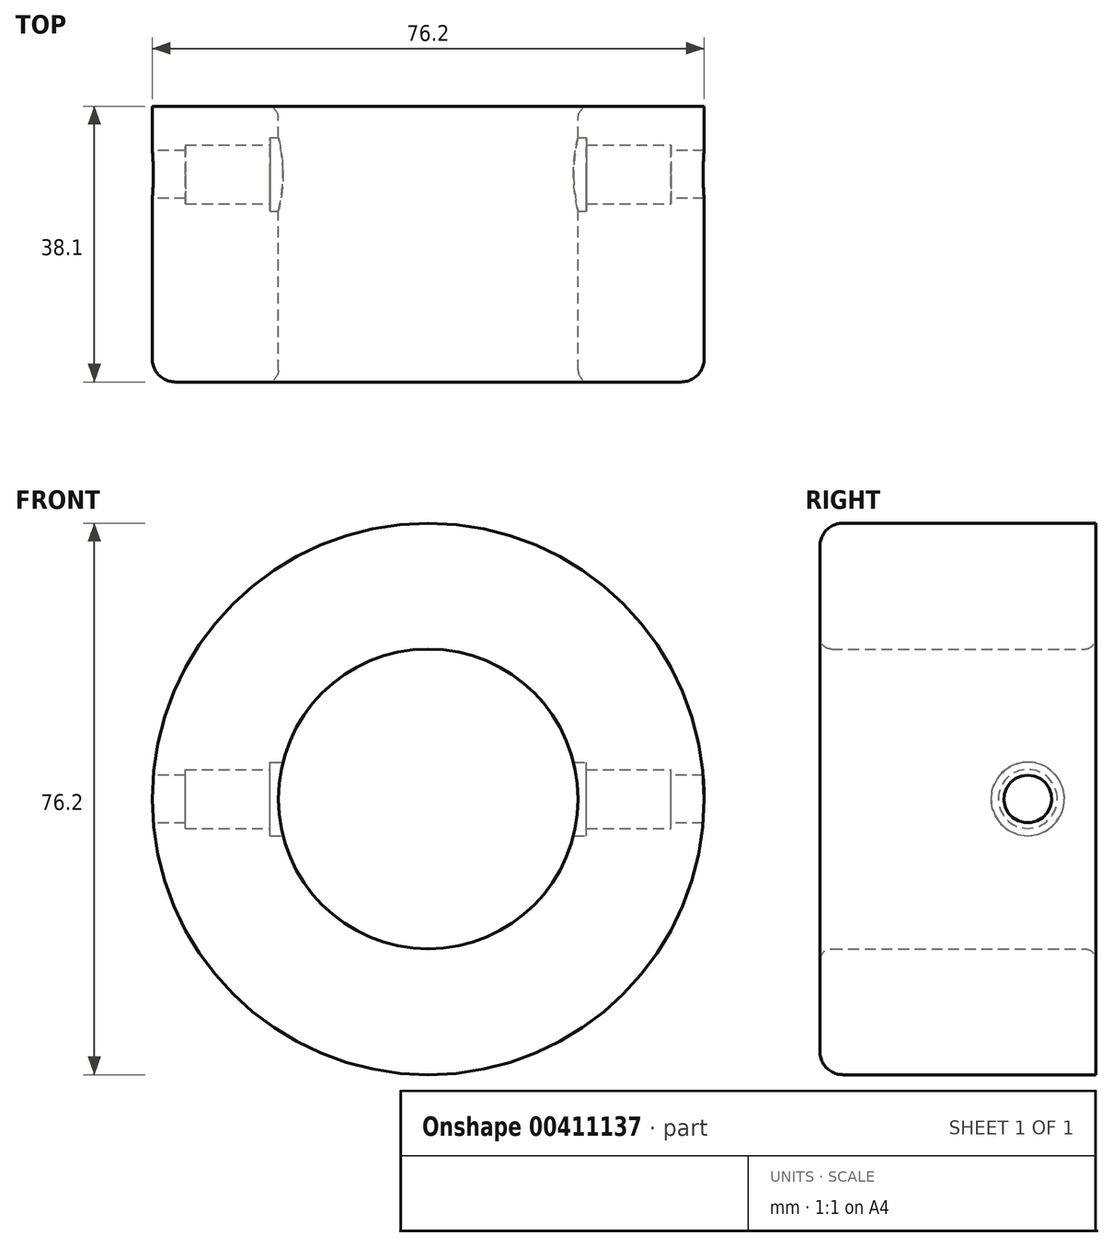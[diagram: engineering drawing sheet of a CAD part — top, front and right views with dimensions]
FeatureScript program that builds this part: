
annotation { "Feature Type Name" : "Feature", "Feature Type Description" : "" }
export const myFeature = defineFeature(function(context is Context, id is Id, definition is map)
    precondition{}
    {
        {
            var Q0;
            Q0=qCreatedBy(makeId("Front.planeOp"),FACE);
            var sketch = newSketch(context, id + "F0", { "sketchPlane" : qUnion([Q0])});
            skCircle(sketch, "E0", {"center": v(0, 0) * mm, "radius": 20.7 * mm});
            skCircle(sketch, "E1", {"center": v(0, 0) * mm, "radius": 38.1 * mm});
            skCircle(sketch, "E2", {"center": v(0, 0) * mm, "radius": 50.8 * mm});
            skSolve(sketch);
        }
        {
            var Q0;
            Q0=makeQuery(id+"F0.imprint","IMPRINT",FACE,{"disambiguationData":[TD([[makeQuery(id+"F0.imprint","IMPRINT",EDGE,{"derivedFrom":sQuery(id+"F0.wireOp",EDGE,"E0")}),-1.0]])]});
            extrude(context, id + "F1", {"entities" : qUnion([Q0]), "depth" : 38.1 * mm});
        }
        {
            var Q0;
            Q0=makeQuery(id+"F1.opExtrude","CAP_EDGE",EDGE,{"disambiguationData":[OSD([sQuery(id+"F0.wireOp",EDGE,"E1")])],"isStart":false});
            fillet(context, id + "F2", {"entities" : qUnion([Q0]), "radius" : 3.17 * mm, "tangentPropagation" : true, "allowEdgeOverflow" : false});
        }
        {
            var Q0;
            Q0=qCreatedBy(makeId("Right.planeOp"),FACE);
            var sketch = newSketch(context, id + "F3", { "sketchPlane" : qUnion([Q0])});
            skCircle(sketch, "E3", {"center": v(-9.4, 0) * mm, "radius": 3.3 * mm});
            skCircle(sketch, "E4", {"center": v(-9.4, 0) * mm, "radius": 4.06 * mm});
            skCircle(sketch, "E5", {"center": v(-9.4, 0) * mm, "radius": 5.08 * mm});
            skSolve(sketch);
        }
        {
            var Q0;
            Q0=makeQuery(id+"F3.imprint","IMPRINT",FACE,{"disambiguationData":[TD([[makeQuery(id+"F3.imprint","IMPRINT",EDGE,{"derivedFrom":sQuery(id+"F3.wireOp",EDGE,"E3")}),1.0]])]});
            extrude(context, id + "F4", {"entities" : qUnion([Q0]), "operationType" : NewBodyOperationType.REMOVE, "endBound" : BoundingType.SYMMETRIC, "depth" : 101.6 * mm});
        }
        {
            var Q0;
            Q0=makeQuery(id+"F3.imprint","IMPRINT",FACE,{"disambiguationData":[TD([[makeQuery(id+"F3.imprint","IMPRINT",EDGE,{"derivedFrom":sQuery(id+"F3.wireOp",EDGE,"E3")}),-1.0]])]});
            extrude(context, id + "F5", {"entities" : qUnion([Q0]), "operationType" : NewBodyOperationType.REMOVE, "endBound" : BoundingType.SYMMETRIC, "oppositeDirection" : true, "depth" : 67.06 * mm});
        }
        {
            var Q0;
            Q0=makeQuery(id+"F3.imprint","IMPRINT",FACE,{"disambiguationData":[TD([[makeQuery(id+"F3.imprint","IMPRINT",EDGE,{"derivedFrom":sQuery(id+"F3.wireOp",EDGE,"E4")}),-1.0]])]});
            extrude(context, id + "F6", {"entities" : qUnion([Q0]), "operationType" : NewBodyOperationType.REMOVE, "endBound" : BoundingType.SYMMETRIC, "oppositeDirection" : true, "depth" : 43.69 * mm});
        }
        {
            var Q0;
            Q0=makeQuery(id+"F1.opExtrude","CAP_EDGE",EDGE,{"disambiguationData":[OSD([sQuery(id+"F0.wireOp",EDGE,"E0")])],"isStart":false});
            var Q1;
            Q1=makeQuery(id+"F1.opExtrude","CAP_EDGE",EDGE,{"disambiguationData":[OSD([sQuery(id+"F0.wireOp",EDGE,"E0")])],"isStart":true});
            fillet(context, id + "F7", {"entities" : qUnion([Q0, Q1]), "radius" : 1.6 * mm, "tangentPropagation" : true, "allowEdgeOverflow" : false});
        }
    });
